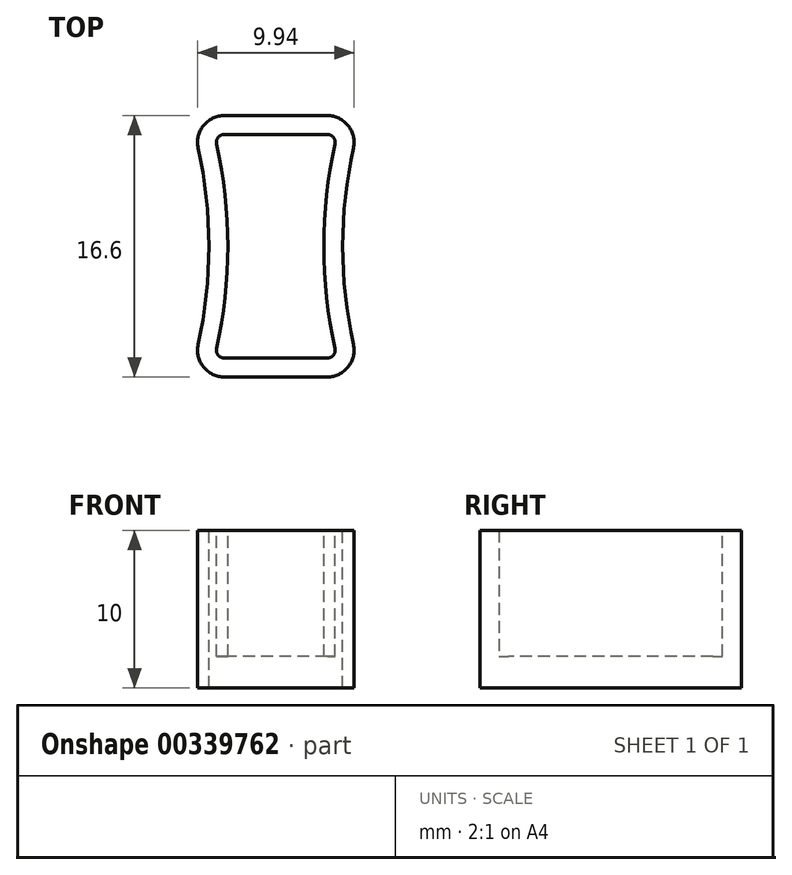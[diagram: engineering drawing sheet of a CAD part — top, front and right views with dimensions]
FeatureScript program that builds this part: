
annotation { "Feature Type Name" : "Feature", "Feature Type Description" : "" }
export const myFeature = defineFeature(function(context is Context, id is Id, definition is map)
    precondition{}
    {
        {
            var Q0;
            Q0=qCreatedBy(makeId("Top.planeOp"),FACE);
            var sketch = newSketch(context, id + "F0", { "sketchPlane" : qUnion([Q0])});
            skCircle(sketch, "E0", {"center": v(0, 0) * mm, "radius": 9 * mm, "construction": true});
            skLineSegment(sketch, "E1.bottom", {"start": v(7, 10) * mm, "end": v(-7, 10) * mm});
            skLineSegment(sketch, "E1.top", {"start": v(7, -10) * mm, "end": v(-7, -10) * mm});
            skLineSegment(sketch, "E1.left", {"start": v(7, 10) * mm, "end": v(7, -10) * mm});
            skLineSegment(sketch, "E1.right", {"start": v(-7, 10) * mm, "end": v(-7, -10) * mm});
            skSolve(sketch);
        }
        {
            var Q0;
            Q0 = qSketchRegion(id + "F0", true);
            extrude(context, id + "F1", {"entities" : qUnion([Q0]), "depth" : 10 * mm});
        }
        {
            var Q0;
            Q0=makeQuery(id+"F1.opExtrude","CAP_FACE",FACE,{"disambiguationData":[OSD([sQuery(id+"F0.wireOp",EDGE,"E1.bottom"),sQuery(id+"F0.wireOp",EDGE,"E1.top"),sQuery(id+"F0.wireOp",EDGE,"E1.left"),sQuery(id+"F0.wireOp",EDGE,"E1.right")])],"isStart":false});
            var sketch = newSketch(context, id + "F2", { "sketchPlane" : qUnion([Q0])});
            skLineSegment(sketch, "E2.bottom", {"start": v(3.9, 7.1) * mm, "end": v(-3.9, 7.1) * mm});
            skLineSegment(sketch, "E2.top", {"start": v(3.9, -7.1) * mm, "end": v(-3.9, -7.1) * mm});
            skLineSegment(sketch, "E2.left", {"start": v(3.9, 7.1) * mm, "end": v(3.9, -7.1) * mm});
            skLineSegment(sketch, "E2.right", {"start": v(-3.9, 7.1) * mm, "end": v(-3.9, -7.1) * mm});
            skPoint(sketch, "E2.middle", {"position": v(0, 0) * mm});
            skCircle(sketch, "E3", {"center": v(33.13, 0) * mm, "radius": 30.08 * mm});
            skCircle(sketch, "E4", {"center": v(-33.13, 0) * mm, "radius": 30.08 * mm});
            skSolve(sketch);
        }
        {
            var Q0;
            {var subQ0=sQuery(id+"F2.wireOp",EDGE,"E2.bottom");Q0=makeQuery(id+"F2.imprint","IMPRINT",FACE,{"disambiguationData":[TD([[makeQuery(id+"F2.imprint","IMPRINT",EDGE,{"derivedFrom":subQ0}),1.0]])]});}
            extrude(context, id + "F3", {"entities" : qUnion([Q0]), "operationType" : NewBodyOperationType.REMOVE, "oppositeDirection" : true, "depth" : 8 * mm});
        }
        {
            var Q0;
            Q0=makeQuery(id+"F3.boolean.opBoolean","COPY",EDGE,{"derivedFrom":makeQuery(id+"F3.opExtrude","SWEPT_EDGE",EDGE,{"disambiguationData":[OSD([sQuery(id+"F2.wireOp",EDGE,"E2.bottom"),sQuery(id+"F2.wireOp",EDGE,"E2.right"),sQuery(id+"F2.wireOp",EDGE,"E4")])]})});
            var Q1;
            Q1=makeQuery(id+"F3.boolean.opBoolean","COPY",EDGE,{"derivedFrom":makeQuery(id+"F3.opExtrude","SWEPT_EDGE",EDGE,{"disambiguationData":[OSD([sQuery(id+"F2.wireOp",EDGE,"E2.top"),sQuery(id+"F2.wireOp",EDGE,"E2.right"),sQuery(id+"F2.wireOp",EDGE,"E4")])]})});
            var Q2;
            Q2=makeQuery(id+"F3.boolean.opBoolean","COPY",EDGE,{"derivedFrom":makeQuery(id+"F3.opExtrude","SWEPT_EDGE",EDGE,{"disambiguationData":[OSD([sQuery(id+"F2.wireOp",EDGE,"E2.bottom"),sQuery(id+"F2.wireOp",EDGE,"E2.left"),sQuery(id+"F2.wireOp",EDGE,"E3")])]})});
            var Q3;
            Q3=makeQuery(id+"F3.boolean.opBoolean","COPY",EDGE,{"derivedFrom":makeQuery(id+"F3.opExtrude","SWEPT_EDGE",EDGE,{"disambiguationData":[OSD([sQuery(id+"F2.wireOp",EDGE,"E2.top"),sQuery(id+"F2.wireOp",EDGE,"E2.left"),sQuery(id+"F2.wireOp",EDGE,"E3")])]})});
            fillet(context, id + "F4", {"entities" : qUnion([Q0, Q1, Q2, Q3]), "radius" : 0.5 * mm, "tangentPropagation" : true, "allowEdgeOverflow" : false});
        }
        {
            var Q0;
            Q0=makeQuery(id+"F1.opExtrude","CAP_FACE",FACE,{"disambiguationData":[OSD([sQuery(id+"F0.wireOp",EDGE,"E1.bottom"),sQuery(id+"F0.wireOp",EDGE,"E1.top"),sQuery(id+"F0.wireOp",EDGE,"E1.left"),sQuery(id+"F0.wireOp",EDGE,"E1.right")])],"isStart":false});
            var sketch = newSketch(context, id + "F5", { "sketchPlane" : qUnion([Q0])});
            skArc(sketch, "E5.0", {"start": v(3.27, -8.3) * mm, "mid": v(4.6, -7.66) * mm, "end": v(4.93, -6.23) * mm});
            skLineSegment(sketch, "E5.1", {"start": v(-3.27, -8.3) * mm, "end": v(3.27, -8.3) * mm});
            skArc(sketch, "E5.2", {"start": v(4.93, -6.23) * mm, "mid": v(4.25, 0) * mm, "end": v(4.93, 6.23) * mm});
            skArc(sketch, "E5.3", {"start": v(-4.93, -6.23) * mm, "mid": v(-4.6, -7.66) * mm, "end": v(-3.27, -8.3) * mm});
            skArc(sketch, "E5.4", {"start": v(4.93, 6.23) * mm, "mid": v(4.6, 7.66) * mm, "end": v(3.27, 8.3) * mm});
            skLineSegment(sketch, "E5.5", {"start": v(3.27, 8.3) * mm, "end": v(-3.27, 8.3) * mm});
            skArc(sketch, "E5.6", {"start": v(-3.27, 8.3) * mm, "mid": v(-4.6, 7.66) * mm, "end": v(-4.93, 6.23) * mm});
            skArc(sketch, "E5.7", {"start": v(-4.93, 6.23) * mm, "mid": v(-4.25, 0) * mm, "end": v(-4.93, -6.23) * mm});
            skSolve(sketch);
        }
        {
            var Q0;
            Q0=makeQuery(id+"F5.imprint","IMPRINT",FACE,{"disambiguationData":[TD([[makeQuery(id+"F5.imprint","IMPRINT",EDGE,{"derivedFrom":sQuery(id+"F5.wireOp",EDGE,"E5.0")}),-1.0]])]});
            extrude(context, id + "F6", {"entities" : qUnion([Q0]), "operationType" : NewBodyOperationType.REMOVE, "endBound" : BoundingType.UP_TO_NEXT, "oppositeDirection" : true, "depth" : 25 * mm});
        }
    });
